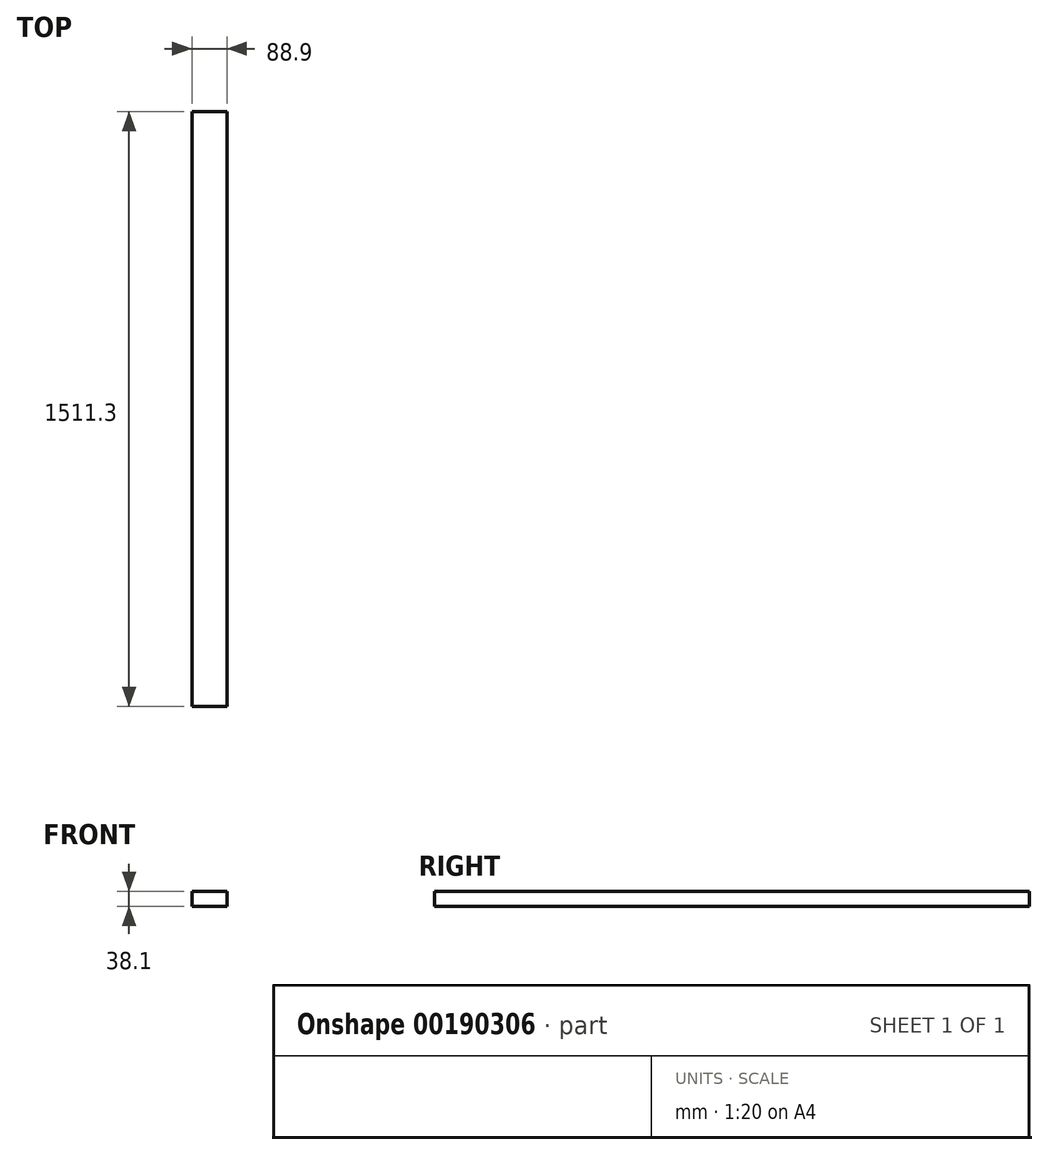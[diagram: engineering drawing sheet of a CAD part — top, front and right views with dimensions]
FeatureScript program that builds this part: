
annotation { "Feature Type Name" : "Feature", "Feature Type Description" : "" }
export const myFeature = defineFeature(function(context is Context, id is Id, definition is map)
    precondition{}
    {
        {
            var Q0;
            Q0=qCreatedBy(makeId("Front.planeOp"),FACE);
            var sketch = newSketch(context, id + "F0", { "sketchPlane" : qUnion([Q0])});
            skLineSegment(sketch, "E0.bottom", {"start": v(44.45, -19.05) * mm, "end": v(-44.45, -19.05) * mm});
            skLineSegment(sketch, "E0.top", {"start": v(44.45, 19.05) * mm, "end": v(-44.45, 19.05) * mm});
            skLineSegment(sketch, "E0.left", {"start": v(44.45, -19.05) * mm, "end": v(44.45, 19.05) * mm});
            skLineSegment(sketch, "E0.right", {"start": v(-44.45, -19.05) * mm, "end": v(-44.45, 19.05) * mm});
            skPoint(sketch, "E0.middle", {"position": v(0, 0) * mm});
            skSolve(sketch);
        }
        {
            var Q0;
            Q0=makeQuery(id+"F0.imprint","IMPRINT",FACE,{"disambiguationData":[TD([[makeQuery(id+"F0.imprint","IMPRINT",EDGE,{"derivedFrom":sQuery(id+"F0.wireOp",EDGE,"E0.bottom")}),-1.0]])]});
            extrude(context, id + "F1", {"entities" : qUnion([Q0]), "depth" : 1511.3 * mm});
        }
    });
